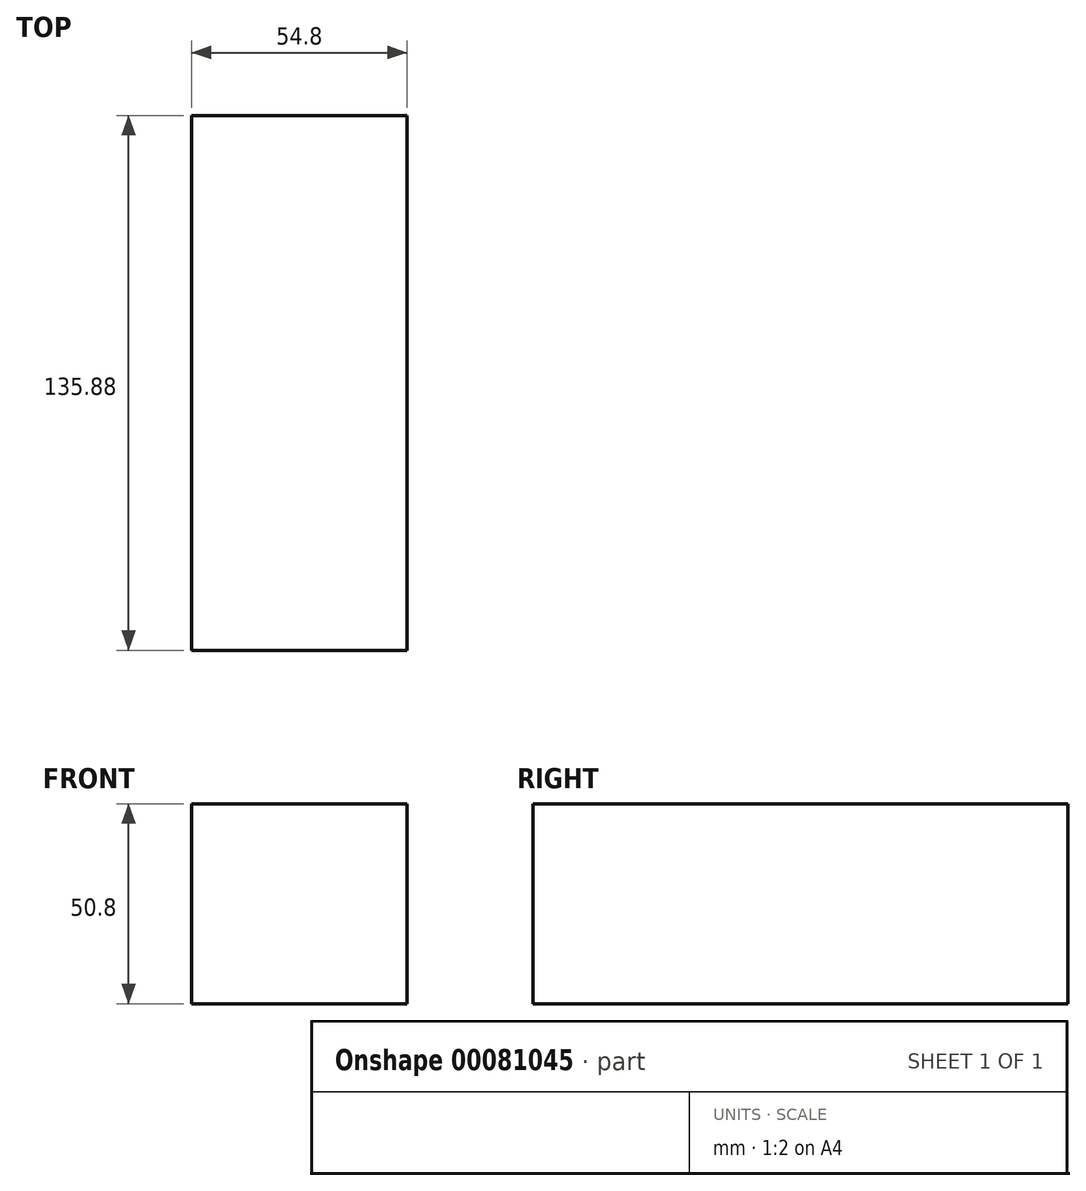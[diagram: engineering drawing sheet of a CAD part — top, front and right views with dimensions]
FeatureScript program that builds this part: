
annotation { "Feature Type Name" : "Feature", "Feature Type Description" : "" }
export const myFeature = defineFeature(function(context is Context, id is Id, definition is map)
    precondition{}
    {
        {
            var Q0;
            Q0=qCreatedBy(makeId("Top.planeOp"),FACE);
            var sketch = newSketch(context, id + "F0", { "sketchPlane" : qUnion([Q0])});
            skLineSegment(sketch, "E0.bottom", {"start": v(-27.4, 67.94) * mm, "end": v(27.4, 67.94) * mm});
            skLineSegment(sketch, "E0.top", {"start": v(-27.4, -67.94) * mm, "end": v(27.4, -67.94) * mm});
            skLineSegment(sketch, "E0.left", {"start": v(-27.4, 67.94) * mm, "end": v(-27.4, -67.94) * mm});
            skLineSegment(sketch, "E0.right", {"start": v(27.4, 67.94) * mm, "end": v(27.4, -67.94) * mm});
            skPoint(sketch, "E0.middle", {"position": v(0, 0) * mm});
            skSolve(sketch);
        }
        {
            var Q0;
            Q0 = qSketchRegion(id + "F0", true);
            extrude(context, id + "F1", {"entities" : qUnion([Q0]), "depth" : 50.8 * mm, "offsetDistance" : 25.4 * mm});
        }
    });
